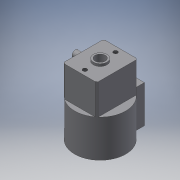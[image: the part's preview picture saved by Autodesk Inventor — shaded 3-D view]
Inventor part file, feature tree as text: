
AUTODESK INVENTOR PART (.ipt)
format: ipt  version: 2019 (Build 230136000, 136)  size: 174,080 bytes
history: native  units: in
note: dims shown in document units (in); Inventor stores cm internally (conversion verified against a paired STEP export)
features: sketch x6, extrude x5, hole x1
ambient origin geometry x8: Origin, YZ Plane, XZ Plane, XY Plane, X Axis, Y Axis, Z Axis, Center Point
bodies: Solid2 (feature_tree)
feature tree (12):
  extrude  "Extrusion3"  Depth=0.1181in
  extrude  "Extrusion4"  Depth=0.3937in
  extrude  "Extrusion5"  Depth=0.7874in TaperAngle=0.0deg
  hole  "Hole1"  [1 undecoded]
  extrude  "Extrusion6"  Depth=1.1811in
  extrude  "Extrusion7"  Depth=0.0276in
  sketch  "Sketch1"  dims[d0=0.5906in d1=0.1181in]
  sketch  "Sketch3"  dims[d2=0.3937in d4=0.3937in]
  sketch  "Sketch4"  dims[d15=0.1181in d16=0.7874in d17=0.0in]
  sketch  "Sketch5"  dims[d18=0.3937in d19=0.4724in]
  sketch  "Sketch6"  dims[d20=1.1811in d21=1.1811in]
  sketch  "Sketch7"  dims[d22=0.5906in d23=0.5906in d24=0.3543in d25=0.0in d26=0.0787in d27=0.0984in d28=0.0984in d29=0.0984in d30=0.0787in d31=0.0512in d32=0.3543in d33=0.0in d34=0.3543in d35=0.1772in d36=0.0481in d37=0.126in d38=0.1575in d39=0.0787in d40=90.0deg d41=0.2087in d42=0.8108in d43=0.2362in d44=0.0394in d45=0.0in d46=0.1575in d47=0.0276in d48=0.0in]
note: 1 required parameter value undecoded (feature->parameter linkage not recoverable at this tier; creation-order binding heuristic only, values carry confidence <= 0.55)
